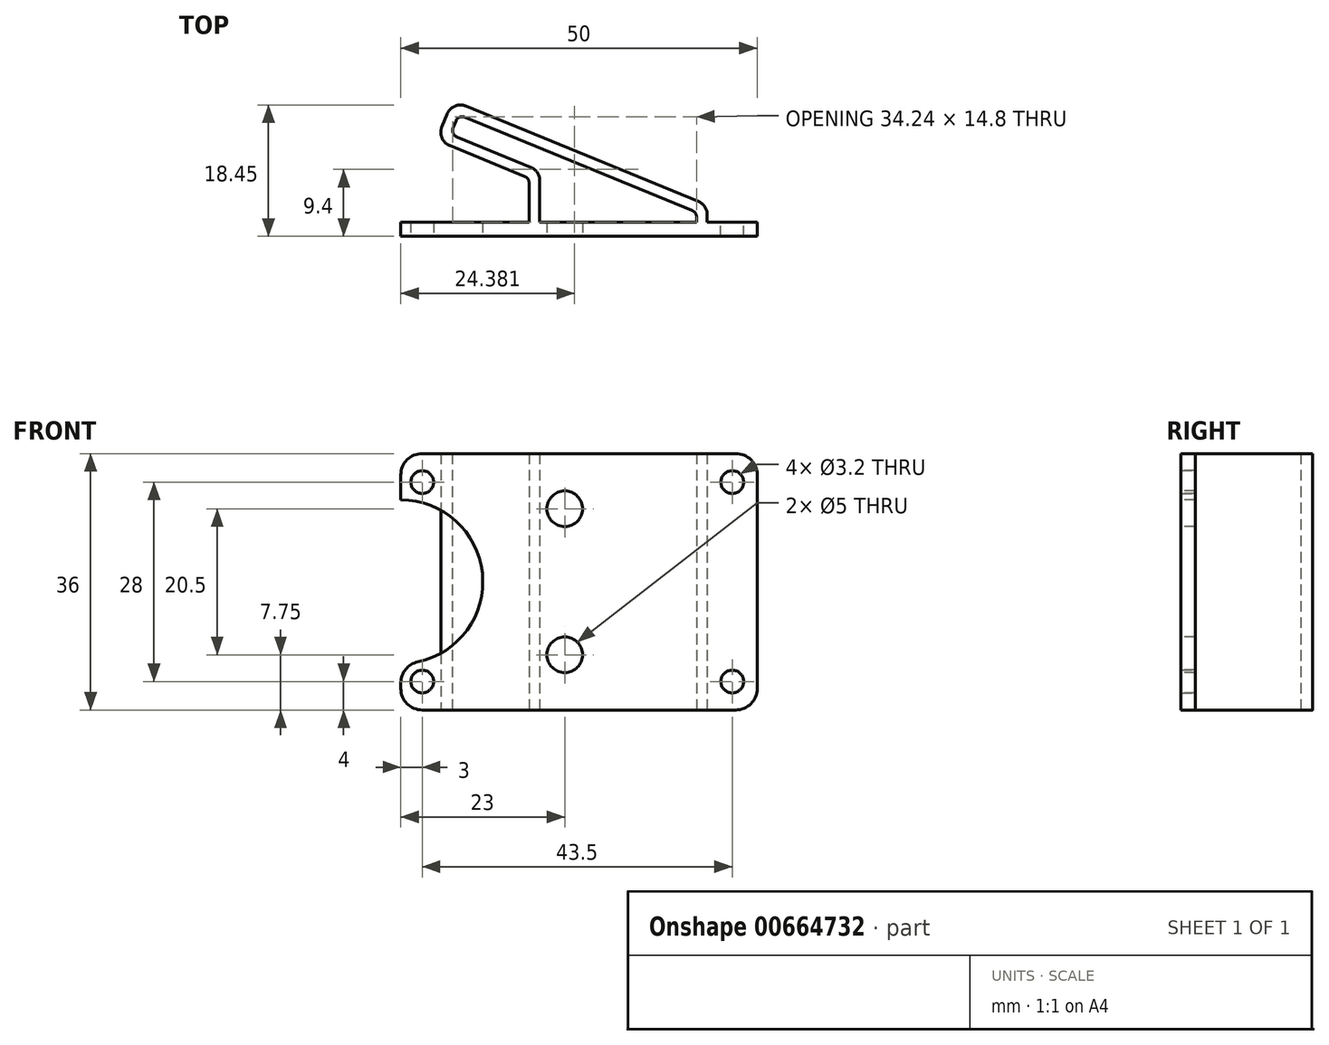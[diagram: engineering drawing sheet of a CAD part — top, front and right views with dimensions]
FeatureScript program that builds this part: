
annotation { "Feature Type Name" : "Feature", "Feature Type Description" : "" }
export const myFeature = defineFeature(function(context is Context, id is Id, definition is map)
    precondition{}
    {
        {
            var Q0;
            Q0=qCreatedBy(makeId("Top.planeOp"),FACE);
            var sketch = newSketch(context, id + "F0", { "sketchPlane" : qUnion([Q0])});
            skLineSegment(sketch, "E0", {"start": v(20, 0) * mm, "end": v(20, 1.5) * mm});
            skLineSegment(sketch, "E1", {"start": v(20, 1.5) * mm, "end": v(13, 1.5) * mm});
            skLineSegment(sketch, "E2", {"start": v(13, 4.38) * mm, "end": v(-22.72, 19.06) * mm});
            skLineSegment(sketch, "E3", {"start": v(13, 1.5) * mm, "end": v(13, 4.38) * mm});
            skPoint(sketch, "E4.start.orphan", {"position": v(-12, 0) * mm});
            skLineSegment(sketch, "E5", {"start": v(-12, 0) * mm, "end": v(20, 0) * mm});
            skLineSegment(sketch, "E6", {"start": v(-12, 1.5) * mm, "end": v(-12, 8.17) * mm});
            skLineSegment(sketch, "E7", {"start": v(-12, 8.17) * mm, "end": v(-25, 13.52) * mm});
            skLineSegment(sketch, "E8", {"start": v(-25, 13.52) * mm, "end": v(-22.72, 19.06) * mm});
            skPoint(sketch, "E9.start.orphan", {"position": v(-30, 0) * mm});
            skLineSegment(sketch, "E10", {"start": v(-12, 0) * mm, "end": v(-30, 0) * mm});
            skLineSegment(sketch, "E11", {"start": v(-30, 1.5) * mm, "end": v(-12, 1.5) * mm});
            skLineSegment(sketch, "E12", {"start": v(-30, 1.5) * mm, "end": v(-30, 0) * mm});
            skSolve(sketch);
        }
        {
            var Q0;
            Q0=makeQuery(id+"F0.imprint","IMPRINT",FACE,{"disambiguationData":[TD([[makeQuery(id+"F0.imprint","IMPRINT",EDGE,{"derivedFrom":sQuery(id+"F0.wireOp",EDGE,"E0")}),1.0]])]});
            extrude(context, id + "F1", {"entities" : qUnion([Q0]), "depth" : 36 * mm, "offsetDistance" : 25 * mm});
        }
        {
            var Q0;
            Q0=makeQuery(id+"F1.opExtrude","CAP_FACE",FACE,{"disambiguationData":[OSD([sQuery(id+"F0.wireOp",EDGE,"E0"),sQuery(id+"F0.wireOp",EDGE,"E1"),sQuery(id+"F0.wireOp",EDGE,"E2"),sQuery(id+"F0.wireOp",EDGE,"E3"),sQuery(id+"F0.wireOp",EDGE,"E5"),sQuery(id+"F0.wireOp",EDGE,"E6"),sQuery(id+"F0.wireOp",EDGE,"E7"),sQuery(id+"F0.wireOp",EDGE,"E8")])],"isStart":false});
            var Q1;
            Q1=makeQuery(id+"F1.opExtrude","CAP_FACE",FACE,{"disambiguationData":[OSD([sQuery(id+"F0.wireOp",EDGE,"E0"),sQuery(id+"F0.wireOp",EDGE,"E1"),sQuery(id+"F0.wireOp",EDGE,"E2"),sQuery(id+"F0.wireOp",EDGE,"E3"),sQuery(id+"F0.wireOp",EDGE,"E5"),sQuery(id+"F0.wireOp",EDGE,"E6"),sQuery(id+"F0.wireOp",EDGE,"E7"),sQuery(id+"F0.wireOp",EDGE,"E8")])],"isStart":true});
            shell(context, id + "F2", {"entities" : qUnion([Q0, Q1]), "thickness" : 1.5 * mm});
        }
        {
            var Q0;
            Q0=makeQuery(id+"F1.opExtrude","SWEPT_FACE",FACE,{"disambiguationData":[OSD([sQuery(id+"F0.wireOp",EDGE,"E1")])]});
            var sketch = newSketch(context, id + "F3", { "sketchPlane" : qUnion([Q0])});
            skCircle(sketch, "E13", {"center": v(-16.5, 32) * mm, "radius": 1.6 * mm});
            skCircle(sketch, "E14", {"center": v(-16.5, 4) * mm, "radius": 1.6 * mm});
            skSolve(sketch);
        }
        {
            var Q0;
            Q0=makeQuery(id+"F3.imprint","IMPRINT",FACE,{"disambiguationData":[TD([[makeQuery(id+"F3.imprint","IMPRINT",EDGE,{"derivedFrom":sQuery(id+"F3.wireOp",EDGE,"E13")}),1.0]])]});
            var Q1;
            Q1=makeQuery(id+"F3.imprint","IMPRINT",FACE,{"disambiguationData":[TD([[makeQuery(id+"F3.imprint","IMPRINT",EDGE,{"derivedFrom":sQuery(id+"F3.wireOp",EDGE,"E14")}),1.0]])]});
            extrude(context, id + "F4", {"entities" : qUnion([Q0, Q1]), "operationType" : NewBodyOperationType.REMOVE, "oppositeDirection" : true, "depth" : 1.5 * mm, "offsetDistance" : 25 * mm});
        }
        {
            var Q0;
            Q0=makeQuery(id+"F1.opExtrude","SWEPT_FACE",FACE,{"disambiguationData":[OSD([sQuery(id+"F0.wireOp",EDGE,"E5"),sQuery(id+"F0.wireOp",EDGE,"E10")])]});
            var sketch = newSketch(context, id + "F5", { "sketchPlane" : qUnion([Q0])});
            skCircle(sketch, "E15", {"center": v(-27, 32) * mm, "radius": 1.6 * mm});
            skCircle(sketch, "E16", {"center": v(-27, 4) * mm, "radius": 1.6 * mm});
            skArc(sketch, "E17", {"start": v(-30, 6.5) * mm, "mid": v(-18.5, 18) * mm, "end": v(-30, 29.5) * mm});
            skCircle(sketch, "E18", {"center": v(-7, 28.25) * mm, "radius": 2.5 * mm});
            skCircle(sketch, "E19", {"center": v(-7, 7.75) * mm, "radius": 2.5 * mm});
            skSolve(sketch);
        }
        {
            var Q0;
            Q0=makeQuery(id+"F5.imprint","IMPRINT",FACE,{"disambiguationData":[TD([[makeQuery(id+"F5.imprint","IMPRINT",EDGE,{"derivedFrom":sQuery(id+"F5.wireOp",EDGE,"E15")}),1.0]])]});
            var Q1;
            {var subQ0=sQuery(id+"F5.wireOp",EDGE,"E17");Q1=makeQuery(id+"F5.imprint","IMPRINT",FACE,{"disambiguationData":[TD([[makeQuery(id+"F5.imprint","IMPRINT",EDGE,{"derivedFrom":subQ0}),1.0]])]});}
            var Q2;
            Q2=makeQuery(id+"F5.imprint","IMPRINT",FACE,{"disambiguationData":[TD([[makeQuery(id+"F5.imprint","IMPRINT",EDGE,{"derivedFrom":sQuery(id+"F5.wireOp",EDGE,"E16")}),1.0]])]});
            extrude(context, id + "F6", {"entities" : qUnion([Q0, Q1, Q2]), "operationType" : NewBodyOperationType.REMOVE, "oppositeDirection" : true, "depth" : 5 * mm, "offsetDistance" : 25 * mm});
        }
        {
            var Q0;
            Q0=makeQuery(id+"F1.opExtrude","SWEPT_FACE",FACE,{"disambiguationData":[OSD([sQuery(id+"F0.wireOp",EDGE,"E1")])]});
            var Q1;
            Q1=makeQuery(id+"F1.opExtrude","SWEPT_FACE",FACE,{"disambiguationData":[OSD([sQuery(id+"F0.wireOp",EDGE,"E11")])]});
            extrude(context, id + "F7", {"entities" : qUnion([Q0, Q1]), "operationType" : NewBodyOperationType.ADD, "depth" : 0.5 * mm, "offsetDistance" : 25 * mm});
        }
        {
            var Q0;
            Q0=makeQuery(id+"F2.opShell","OFFSET_FACE",FACE,{"disambiguationData":[OSD([sQuery(id+"F0.wireOp",EDGE,"E5"),sQuery(id+"F0.wireOp",EDGE,"E10")])]});
            extrude(context, id + "F8", {"entities" : qUnion([Q0]), "operationType" : NewBodyOperationType.ADD, "depth" : 0.5 * mm, "offsetDistance" : 25 * mm});
        }
        {
            var Q0;
            {var subQ0=sQuery(id+"F0.wireOp",EDGE,"E1");var subQ1=sQuery(id+"F0.wireOp",EDGE,"E0");Q0=makeQuery(id+"F7.boolean.opBoolean","MERGE",EDGE,{"derivedFrom":[makeQuery(id+"F1.opExtrude","CAP_EDGE",EDGE,{"disambiguationData":[OSD([subQ1])],"isStart":false}),makeQuery(id+"F7.opExtrude","SWEPT_EDGE",EDGE,{"disambiguationData":[OSD([subQ1,subQ0]),TDD([makeQuery(id+"F1.opExtrude","CAP_VERTEX",VERTEX,{"disambiguationData":[OSD([subQ1,subQ0])],"isStart":false})])]})]});}
            var Q1;
            {var subQ0=sQuery(id+"F0.wireOp",EDGE,"E1");var subQ1=sQuery(id+"F0.wireOp",EDGE,"E0");Q1=makeQuery(id+"F7.boolean.opBoolean","MERGE",EDGE,{"derivedFrom":[makeQuery(id+"F1.opExtrude","CAP_EDGE",EDGE,{"disambiguationData":[OSD([subQ1])],"isStart":true}),makeQuery(id+"F7.opExtrude","SWEPT_EDGE",EDGE,{"disambiguationData":[OSD([subQ1,subQ0]),TDD([makeQuery(id+"F1.opExtrude","CAP_VERTEX",VERTEX,{"disambiguationData":[OSD([subQ1,subQ0])],"isStart":true})])]})]});}
            var Q2;
            {var subQ0=sQuery(id+"F0.wireOp",EDGE,"E12");var subQ1=sQuery(id+"F0.wireOp",EDGE,"E11");Q2=makeQuery(id+"F7.boolean.opBoolean","MERGE",EDGE,{"derivedFrom":[makeQuery(id+"F1.opExtrude","CAP_EDGE",EDGE,{"disambiguationData":[OSD([subQ0])],"isStart":true}),makeQuery(id+"F7.opExtrude","SWEPT_EDGE",EDGE,{"disambiguationData":[OSD([subQ1,subQ0]),TDD([makeQuery(id+"F1.opExtrude","CAP_VERTEX",VERTEX,{"disambiguationData":[OSD([subQ1,subQ0])],"isStart":true})])]})]});}
            var Q3;
            {var subQ0=sQuery(id+"F0.wireOp",EDGE,"E12");var subQ1=sQuery(id+"F0.wireOp",EDGE,"E11");Q3=makeQuery(id+"F7.boolean.opBoolean","MERGE",EDGE,{"derivedFrom":[makeQuery(id+"F1.opExtrude","CAP_EDGE",EDGE,{"disambiguationData":[OSD([subQ0])],"isStart":false}),makeQuery(id+"F7.opExtrude","SWEPT_EDGE",EDGE,{"disambiguationData":[OSD([subQ1,subQ0]),TDD([makeQuery(id+"F1.opExtrude","CAP_VERTEX",VERTEX,{"disambiguationData":[OSD([subQ1,subQ0])],"isStart":false})])]})]});}
            var Q4;
            {var subQ0=sQuery(id+"F5.wireOp",EDGE,"E17");var subQ1=sQuery(id+"F0.wireOp",EDGE,"E11");var subQ2=sQuery(id+"F0.wireOp",EDGE,"E12");var subQ3=sQuery(id+"F0.wireOp",EDGE,"E10");Q4=makeQuery(id+"F7.boolean.opBoolean","MERGE",EDGE,{"derivedFrom":[makeQuery(id+"F6.boolean.opBoolean","COPY",EDGE,{"derivedFrom":makeQuery(id+"F6.opExtrude","SWEPT_EDGE",EDGE,{"disambiguationData":[OSD([subQ3,subQ2,subQ0]),TDD([makeQuery(id+"F5.imprint","INTERSECT",VERTEX,{"disambiguationData":[OD(1.0)],"derivedFrom":[makeQuery(id+"F1.opExtrude","SWEPT_EDGE",EDGE,{"disambiguationData":[OSD([subQ3,subQ2])]}),subQ0]})])]})}),makeQuery(id+"F7.opExtrude","SWEPT_EDGE",EDGE,{"disambiguationData":[OSD([subQ1,subQ0]),TDD([makeQuery(id+"F6.boolean.opBoolean","INTERSECT",VERTEX,{"disambiguationData":[OD(1.0)],"derivedFrom":[makeQuery(id+"F1.opExtrude","SWEPT_FACE",FACE,{"disambiguationData":[OSD([subQ1])]}),makeQuery(id+"F6.opExtrude","SWEPT_FACE",FACE,{"disambiguationData":[OSD([subQ0])]})]})])]})]});}
            var Q5;
            {var subQ0=sQuery(id+"F5.wireOp",EDGE,"E17");var subQ1=sQuery(id+"F0.wireOp",EDGE,"E11");var subQ2=sQuery(id+"F0.wireOp",EDGE,"E12");var subQ3=sQuery(id+"F0.wireOp",EDGE,"E10");Q5=makeQuery(id+"F7.boolean.opBoolean","MERGE",EDGE,{"derivedFrom":[makeQuery(id+"F6.boolean.opBoolean","COPY",EDGE,{"derivedFrom":makeQuery(id+"F6.opExtrude","SWEPT_EDGE",EDGE,{"disambiguationData":[OSD([subQ3,subQ2,subQ0]),TDD([makeQuery(id+"F5.imprint","INTERSECT",VERTEX,{"disambiguationData":[OD(0.0)],"derivedFrom":[makeQuery(id+"F1.opExtrude","SWEPT_EDGE",EDGE,{"disambiguationData":[OSD([subQ3,subQ2])]}),subQ0]})])]})}),makeQuery(id+"F7.opExtrude","SWEPT_EDGE",EDGE,{"disambiguationData":[OSD([subQ1,subQ0]),TDD([makeQuery(id+"F6.boolean.opBoolean","INTERSECT",VERTEX,{"disambiguationData":[OD(0.0)],"derivedFrom":[makeQuery(id+"F1.opExtrude","SWEPT_FACE",FACE,{"disambiguationData":[OSD([subQ1])]}),makeQuery(id+"F6.opExtrude","SWEPT_FACE",FACE,{"disambiguationData":[OSD([subQ0])]})]})])]})]});}
            fillet(context, id + "F9", {"entities" : qUnion([Q0, Q1, Q2, Q3, Q4, Q5]), "radius" : 3 * mm, "tangentPropagation" : true, "allowEdgeOverflow" : false});
        }
        {
            var Q0;
            Q0=makeQuery(id+"F8.opExtrude","CAP_EDGE",EDGE,{"disambiguationData":[OSD([sQuery(id+"F0.wireOp",EDGE,"E5"),sQuery(id+"F0.wireOp",EDGE,"E6"),sQuery(id+"F0.wireOp",EDGE,"E10")])],"isStart":false});
            var Q1;
            Q1=makeQuery(id+"F2.opShell","OFFSET_EDGE",EDGE,{"disambiguationData":[OSD([sQuery(id+"F0.wireOp",EDGE,"E7"),sQuery(id+"F0.wireOp",EDGE,"E8")])]});
            var Q2;
            Q2=makeQuery(id+"F2.opShell","OFFSET_EDGE",EDGE,{"disambiguationData":[OSD([sQuery(id+"F0.wireOp",EDGE,"E2"),sQuery(id+"F0.wireOp",EDGE,"E8")])]});
            var Q3;
            Q3=makeQuery(id+"F8.opExtrude","CAP_EDGE",EDGE,{"disambiguationData":[OSD([sQuery(id+"F0.wireOp",EDGE,"E3"),sQuery(id+"F0.wireOp",EDGE,"E5"),sQuery(id+"F0.wireOp",EDGE,"E10")])],"isStart":false});
            var Q4;
            Q4=makeQuery(id+"F2.opShell","OFFSET_EDGE",EDGE,{"disambiguationData":[OSD([sQuery(id+"F0.wireOp",EDGE,"E2"),sQuery(id+"F0.wireOp",EDGE,"E3")])]});
            var Q5;
            Q5=makeQuery(id+"F7.opExtrude","CAP_EDGE",EDGE,{"disambiguationData":[OSD([sQuery(id+"F0.wireOp",EDGE,"E6"),sQuery(id+"F0.wireOp",EDGE,"E11")])],"isStart":false});
            var Q6;
            Q6=makeQuery(id+"F1.opExtrude","SWEPT_EDGE",EDGE,{"disambiguationData":[OSD([sQuery(id+"F0.wireOp",EDGE,"E6"),sQuery(id+"F0.wireOp",EDGE,"E7")])]});
            fillet(context, id + "F10", {"entities" : qUnion([Q0, Q1, Q2, Q3, Q4, Q5, Q6]), "radius" : 1 * mm, "tangentPropagation" : true, "allowEdgeOverflow" : false});
        }
        {
            var Q0;
            Q0=makeQuery(id+"F1.opExtrude","SWEPT_EDGE",EDGE,{"disambiguationData":[OSD([sQuery(id+"F0.wireOp",EDGE,"E7"),sQuery(id+"F0.wireOp",EDGE,"E8")])]});
            var Q1;
            Q1=makeQuery(id+"F1.opExtrude","SWEPT_EDGE",EDGE,{"disambiguationData":[OSD([sQuery(id+"F0.wireOp",EDGE,"E2"),sQuery(id+"F0.wireOp",EDGE,"E8")])]});
            var Q2;
            Q2=makeQuery(id+"F1.opExtrude","SWEPT_EDGE",EDGE,{"disambiguationData":[OSD([sQuery(id+"F0.wireOp",EDGE,"E2"),sQuery(id+"F0.wireOp",EDGE,"E3")])]});
            var Q3;
            Q3=makeQuery(id+"F2.opShell","OFFSET_EDGE",EDGE,{"disambiguationData":[OSD([sQuery(id+"F0.wireOp",EDGE,"E6"),sQuery(id+"F0.wireOp",EDGE,"E7")])]});
            fillet(context, id + "F11", {"entities" : qUnion([Q0, Q1, Q2, Q3]), "radius" : 2 * mm, "tangentPropagation" : true, "allowEdgeOverflow" : false});
        }
        {
            var Q0;
            Q0=makeQuery(id+"F5.imprint","IMPRINT",FACE,{"disambiguationData":[TD([[makeQuery(id+"F5.imprint","IMPRINT",EDGE,{"derivedFrom":sQuery(id+"F5.wireOp",EDGE,"E18")}),1.0]])]});
            var Q1;
            Q1=makeQuery(id+"F5.imprint","IMPRINT",FACE,{"disambiguationData":[TD([[makeQuery(id+"F5.imprint","IMPRINT",EDGE,{"derivedFrom":sQuery(id+"F5.wireOp",EDGE,"E19")}),1.0]])]});
            extrude(context, id + "F12", {"entities" : qUnion([Q0, Q1]), "operationType" : NewBodyOperationType.REMOVE, "oppositeDirection" : true, "depth" : 5 * mm, "offsetDistance" : 25 * mm});
        }
    });
